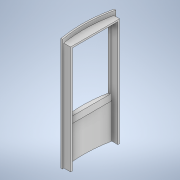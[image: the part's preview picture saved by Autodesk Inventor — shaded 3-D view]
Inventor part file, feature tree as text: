
AUTODESK INVENTOR PART (.ipt)
format: ipt  version: 2022 (Build 260153000, 153)  size: 187,904 bytes
history: native  units: mm
features: extrude x12, fillet x3, sketch x1
ambient origin geometry x8: Origin, YZ Plane, XZ Plane, XY Plane, X Axis, Y Axis, Z Axis, Center Point
bodies: Solid1 (feature_tree)
feature tree (16):
  sketch  "Sketch1"  dims[d14=75.0mm d15=4.5mm d16=68.0mm d17=2.0mm d18=2.0mm d19=2.0mm d20=2.0mm d21=2.0mm d22=32.0mm d23=26.0mm d24=26.0mm d26=28.0mm d27=28.0mm d29=2.0mm d30=7.5mm d31=7.5mm d32=2.0mm d33=138.0mm d34=0.0mm d35=133.0mm d36=0.0mm d37=131.0mm d38=0.0mm d39=129.0mm d40=0.0mm d41=131.0mm d42=0.0mm d43=129.0mm d44=0.0mm d45=51.0mm d46=0.0mm d47=51.0mm d48=0.0mm d49=43.0mm d50=0.0mm d51=41.0mm d52=0.0mm d53=43.0mm d54=0.0mm d55=41.0mm d56=0.0mm d57=1.0mm d58=1.5mm d59=1.5mm d60=0.0mm d61=0.0mm d62=0.0mm]
  extrude  "Extrusion1"  Depth=43.0mm
  extrude  "Extrusion2"  Depth=43.0mm
  extrude  "Extrusion3"  Depth=2.0mm
  extrude  "Extrusion4"  Depth=2.0mm
  extrude  "Extrusion5"  Depth=2.0mm
  extrude  "Extrusion6"  Depth=2.0mm
  extrude  "Extrusion7"  Depth=2.0mm
  extrude  "Extrusion8"  Depth=43.0mm
  extrude  "Extrusion9"  Depth=43.0mm
  extrude  "Extrusion10"  Depth=43.0mm
  extrude  "Extrusion11"  Depth=43.0mm
  extrude  "Extrusion12"  Depth=43.0mm
  fillet  "Fillet1"  Radius=2.0mm
  fillet  "Fillet2"  Radius=7.5mm
  fillet  "Fillet3"  Radius=7.5mm
